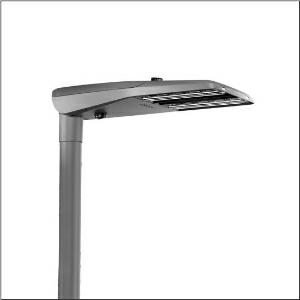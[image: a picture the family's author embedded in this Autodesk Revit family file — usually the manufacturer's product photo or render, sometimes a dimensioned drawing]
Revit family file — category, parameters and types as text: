
# Revit family: streetlight_sl_11_iq_midi___st1_0ab_5xc3n51y08le_be24
name_source: partatom
category: Lighting Fixtures
units: mm (PartAtom-declared; Revit-internal decimal feet)

## family parameters
Cut with Voids When Loaded = No
Host = Face
Light Source = No
Part Type = Normal
Room Calculation Point = No
Round Connector Dimension = Use Diameter
Shared = No

## types (1)
- --- (1 x LED, 7760 lm, 59.4 W, 3000K)
    Apparent Load = 59 VA
    CIE Flux Codes = 29 63 95 100 100
    Color Rendering = 70
    Color Temperature = 3000K
    Default Elevation = 1800 mm
    Description = Streetlight SL 11 iQ midi, mast luminaire, primary light control with 3 zone facetted reflector, of plastic, silver coated, highly specular, primary optical cover: cover, of PMMA, transparent, light distribution: ST1.0aB, light emission: direct distribution, primary light characteristic: asymmetric, installation type: post-top, side-entry, lamps: LED, High Power LED, rated values: 7.760lm | 59,4W | 130,6lm/W (begin service life); end service life: 7.760lm | 61,6W; at 50% lumin. flux: 3.880lm | 28,5W | 136,1lm/W, colour temperature: 3000K, colour rendering: CRI > 70, light colour: 730, light setting 1 begin service life: 100% | 7.760lm | 59,4W | 130,6lm/W | 3.000K, light setting 1 end service life: 61,6W, further light settings possible, control: pre-setting: logarithmic dimming characteristic, Street-Remote, Auto-Match, Temp-Guard, Lumen-Switch, Night-Set, Smart-Wire, Light-Fading, Desk-Remote (wireless, voltage-free reading and setting of iQ features in the workshop via application-optimized NFC function/RFID function), optimised constant luminous flux control (CLO 2.0), with cable H07RN-F 5x 1.5mm², mains connection: 230..240V, AC, 50/60Hz, connection cable pre-assembled, cable length: 8,5m, luminaire housing, of diecast aluminium, powder-coated, Siteco® metallic grey (DB 702S), please order mast flange separately, inclination adjustable without tools: 0°, 5°, 10°, 15° (post-top) | 0°, -5°, -10°, -15° (side-entry), sealing non-destructively replaceable, multi-level sealing system, length: 780mm, width: 376mm, height: 118mm, mast flange for spigot size: 42mm (side-entry): 5XC10008XM4, 60/48mm (side-entry/post-top): 5XC10108XM2, 76/60mm (side-entry/post-top): 5XC10108XM1, equipment: standard, Smart Interface below and above, protection rating (complete): IP66, insulation class (complete): insulation class II (safety insulation), certification: CE, ENEC, ENEC+, VDE, UKCA, impact resistance: IK10, permissible operating ambient temperature for outdoor applications: -25..+50°C, standard-compliant lighting for roads and squares, Environmental Product Declaration (EPD) tested and certified by an independent institute, packaging unit: 1 piece

Light Distribution: ST1.0aB
    Height = 118 mm
    Lamp = 1 x LED
    Lamp Light Flux = 7760 lm
    Lamp Power = 59.4 W
    Lamp count = 1
    Length = 780 mm
    Luminous efficacy = 131 lm/W
    Manufacturer = Siteco
    ModVariant = No
    Model = 5XC3N51Y08LE
    Number of Poles = 1
    OnlyDefault = Yes
    Power Factor = 1
    Product Name = Streetlight SL 11 iQ midi | ST1.0aB
    Product group = mast luminaire | pylon top
    ProductGroupID = 6100
    Protection Class = Protection class II
    Protection Degree = IP 66
    RLX_Detail_Level = 1
    RLX_Emergency_Light_Flux = 0 lm
    RLX_Emergency_Type = 0
    RLX_Emergency_Type_DB = No
    RlxData = <blob elided: 69265 chars, md5=bcecf4ba>
    Socket = socket
    Standby Power = 0 W
    System Light Flux = 7760 lm
    System Power = 59 W
    Type Comments = factory setting: luminous flux: 100 % | dim-lin: 254 | 521 mA
    Type Image = l_1004429.jpg
    URL = http://relux.com
    VarID = @adj_109409
    Voltage = 0 V
    Weight = 0.00 kg
    Width = 376 mm

## geometry (parser evidence)
native form markers: Blend x4, Sweep x12
no freeform markers — native parametric forms only
